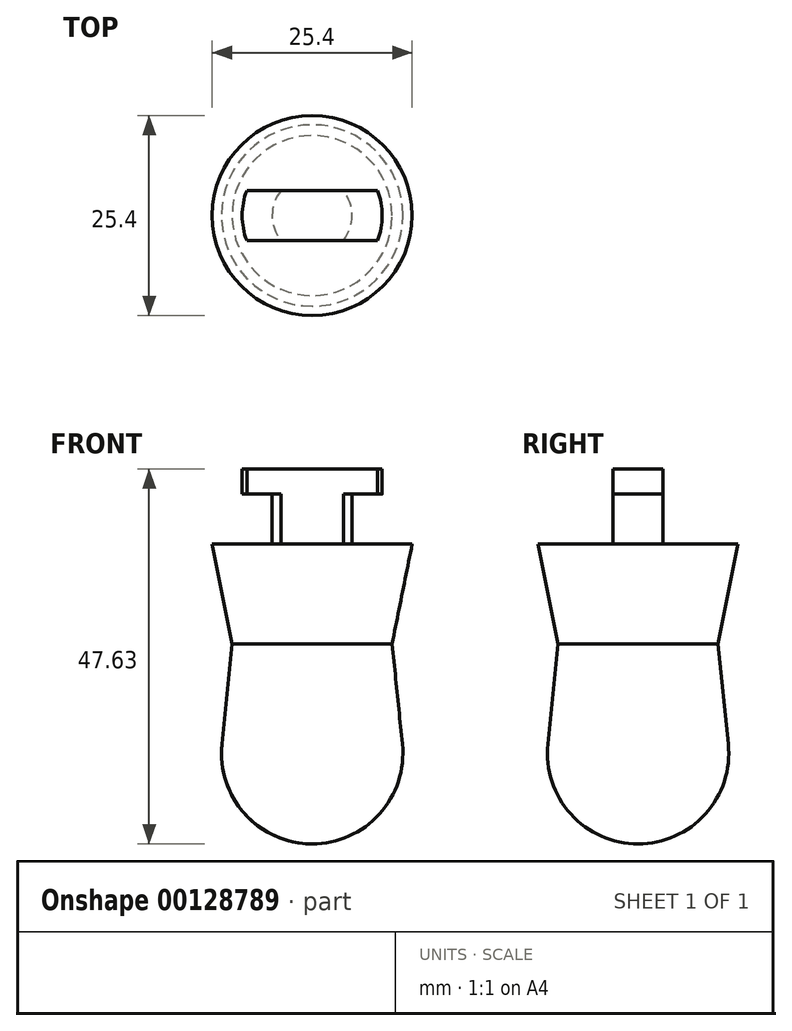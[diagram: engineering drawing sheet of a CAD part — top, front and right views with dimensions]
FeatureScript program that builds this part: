
annotation { "Feature Type Name" : "Feature", "Feature Type Description" : "" }
export const myFeature = defineFeature(function(context is Context, id is Id, definition is map)
    precondition{}
    {
        {
            var Q0;
            Q0=qCreatedBy(makeId("Front.planeOp"),FACE);
            var sketch = newSketch(context, id + "F0", { "sketchPlane" : qUnion([Q0])});
            skLineSegment(sketch, "E0", {"start": v(0, 0) * mm, "end": v(0, -38.1) * mm});
            skLineSegment(sketch, "E1", {"start": v(0, 0) * mm, "end": v(-12.7, 0) * mm});
            skArc(sketch, "E2", {"start": v(-11.46, -25.4) * mm, "mid": v(-8.55, -34.3) * mm, "end": v(0, -38.1) * mm});
            skLineSegment(sketch, "E3", {"start": v(0, -12.7) * mm, "end": v(-10.16, -12.7) * mm});
            skLineSegment(sketch, "E4", {"start": v(-10.16, -12.7) * mm, "end": v(-12.7, 0) * mm});
            skLineSegment(sketch, "E5", {"start": v(-11.46, -25.4) * mm, "end": v(-10.16, -12.7) * mm});
            skLineSegment(sketch, "E6", {"start": v(0, 0) * mm, "end": v(-5.08, 0) * mm});
            skLineSegment(sketch, "E7", {"start": v(-5.08, 0) * mm, "end": v(-5.08, 6.35) * mm});
            skLineSegment(sketch, "E8", {"start": v(-5.08, 6.35) * mm, "end": v(-8.9, 6.35) * mm});
            skLineSegment(sketch, "E9", {"start": v(-8.9, 6.35) * mm, "end": v(-8.9, 9.53) * mm});
            skLineSegment(sketch, "E10", {"start": v(-8.9, 9.53) * mm, "end": v(0, 9.53) * mm});
            skLineSegment(sketch, "E11", {"start": v(0, 9.53) * mm, "end": v(0, 0) * mm});
            skPoint(sketch, "E12", {"position": v(0, -12.7) * mm});
            skLineSegment(sketch, "E13", {"start": v(0, -38.1) * mm, "end": v(16.53, -38.1) * mm, "construction": true});
            skLineSegment(sketch, "E14", {"start": v(0, 0) * mm, "end": v(0, -25.4) * mm});
            skLineSegment(sketch, "E15", {"start": v(-11.46, -25.4) * mm, "end": v(0, -25.4) * mm});
            skSolve(sketch);
        }
        {
            var Q0;
            Q0=qSketchRegion(id+"F0",true);
            var Q1;
            Q1=sQuery(id+"F0.wireOp",EDGE,"E0");
            revolve(context, id + "F1", {"entities" : qUnion([Q0]), "axis" : qUnion([Q1]), "revolveType" : RevolveType.FULL});
        }
        {
            var Q0;
            Q0=makeQuery(id+"F1.opRevolve","SWEPT_FACE",FACE,{"disambiguationData":[OSD([sQuery(id+"F0.wireOp",EDGE,"E10")])]});
            var sketch = newSketch(context, id + "F2", { "sketchPlane" : qUnion([Q0])});
            skLineSegment(sketch, "E16.bottom", {"start": v(-18.75, 3.18) * mm, "end": v(18.75, 3.18) * mm});
            skLineSegment(sketch, "E16.top", {"start": v(-18.75, -3.18) * mm, "end": v(18.75, -3.18) * mm});
            skLineSegment(sketch, "E16.left", {"start": v(-18.75, 3.18) * mm, "end": v(-18.75, -3.18) * mm});
            skLineSegment(sketch, "E16.right", {"start": v(18.75, 3.18) * mm, "end": v(18.75, -3.18) * mm});
            skPoint(sketch, "E16.middle", {"position": v(0, 0) * mm});
            skCircle(sketch, "E17", {"center": v(0, 0) * mm, "radius": 11.42 * mm});
            skSolve(sketch);
        }
        {
            var Q0;
            {var subQ0=sQuery(id+"F2.wireOp",EDGE,"E16.bottom");var subQ1=makeQuery(id+"F1.opRevolve","SWEPT_EDGE",EDGE,{"disambiguationData":[OSD([sQuery(id+"F0.wireOp",EDGE,"E9"),sQuery(id+"F0.wireOp",EDGE,"E10")])]});var subQ2=makeQuery(id+"F2.imprint","INTERSECT",VERTEX,{"disambiguationData":[OD(0.0)],"derivedFrom":[subQ1,subQ0]});Q0=makeQuery(id+"F2.imprint","IMPRINT",FACE,{"disambiguationData":[TD([[makeQuery(id+"F2.imprint","IMPRINT",EDGE,{"disambiguationData":[TD([[subQ2,-1.0]])],"derivedFrom":subQ0}),1.0]])]});}
            var Q1;
            {var subQ0=sQuery(id+"F2.wireOp",EDGE,"E16.top");var subQ1=makeQuery(id+"F1.opRevolve","SWEPT_EDGE",EDGE,{"disambiguationData":[OSD([sQuery(id+"F0.wireOp",EDGE,"E9"),sQuery(id+"F0.wireOp",EDGE,"E10")])]});var subQ2=makeQuery(id+"F2.imprint","INTERSECT",VERTEX,{"disambiguationData":[OD(0.0)],"derivedFrom":[subQ1,subQ0]});Q1=makeQuery(id+"F2.imprint","IMPRINT",FACE,{"disambiguationData":[TD([[makeQuery(id+"F2.imprint","IMPRINT",EDGE,{"disambiguationData":[TD([[subQ2,-1.0]])],"derivedFrom":subQ0}),-1.0]])]});}
            var Q2;
            {var subQ0=sQuery(id+"F2.wireOp",EDGE,"E17");var subQ1=sQuery(id+"F2.wireOp",EDGE,"E16.bottom");var subQ2=makeQuery(id+"F2.imprint","INTERSECT",VERTEX,{"disambiguationData":[OD(0.0)],"derivedFrom":[subQ1,subQ0]});Q2=makeQuery(id+"F2.imprint","IMPRINT",FACE,{"disambiguationData":[TD([[makeQuery(id+"F2.imprint","IMPRINT",EDGE,{"disambiguationData":[TD([[subQ2,1.0]])],"derivedFrom":subQ0}),1.0]])]});}
            var Q3;
            {var subQ0=sQuery(id+"F2.wireOp",EDGE,"E17");var subQ1=sQuery(id+"F2.wireOp",EDGE,"E16.top");var subQ2=makeQuery(id+"F2.imprint","INTERSECT",VERTEX,{"disambiguationData":[OD(0.0)],"derivedFrom":[subQ1,subQ0]});Q3=makeQuery(id+"F2.imprint","IMPRINT",FACE,{"disambiguationData":[TD([[makeQuery(id+"F2.imprint","IMPRINT",EDGE,{"disambiguationData":[TD([[subQ2,-1.0]])],"derivedFrom":subQ0}),1.0]])]});}
            var Q4;
            {var subQ0=sQuery(id+"F2.wireOp",EDGE,"E17");var subQ1=sQuery(id+"F2.wireOp",EDGE,"E16.bottom");var subQ2=makeQuery(id+"F2.imprint","INTERSECT",VERTEX,{"disambiguationData":[OD(0.0)],"derivedFrom":[subQ1,subQ0]});Q4=makeQuery(id+"F2.imprint","IMPRINT",FACE,{"disambiguationData":[TD([[makeQuery(id+"F2.imprint","IMPRINT",EDGE,{"disambiguationData":[TD([[subQ2,-1.0]])],"derivedFrom":subQ0}),1.0]])]});}
            var Q5;
            {var subQ0=sQuery(id+"F2.wireOp",EDGE,"E17");var subQ1=sQuery(id+"F2.wireOp",EDGE,"E16.bottom");var subQ2=makeQuery(id+"F2.imprint","INTERSECT",VERTEX,{"disambiguationData":[OD(1.0)],"derivedFrom":[subQ1,subQ0]});Q5=makeQuery(id+"F2.imprint","IMPRINT",FACE,{"disambiguationData":[TD([[makeQuery(id+"F2.imprint","IMPRINT",EDGE,{"disambiguationData":[TD([[subQ2,1.0]])],"derivedFrom":subQ0}),1.0]])]});}
            var Q6;
            Q6=makeQuery(id+"F1.opRevolve","SWEPT_FACE",FACE,{"disambiguationData":[OSD([sQuery(id+"F0.wireOp",EDGE,"E1")])]});
            extrude(context, id + "F3", {"entities" : qUnion([Q0, Q1, Q2, Q3, Q4, Q5]), "operationType" : NewBodyOperationType.REMOVE, "endBound" : BoundingType.UP_TO_SURFACE, "oppositeDirection" : true, "endBoundEntityFace" : qUnion([Q6]), "depth" : 25.4 * mm});
        }
    });
